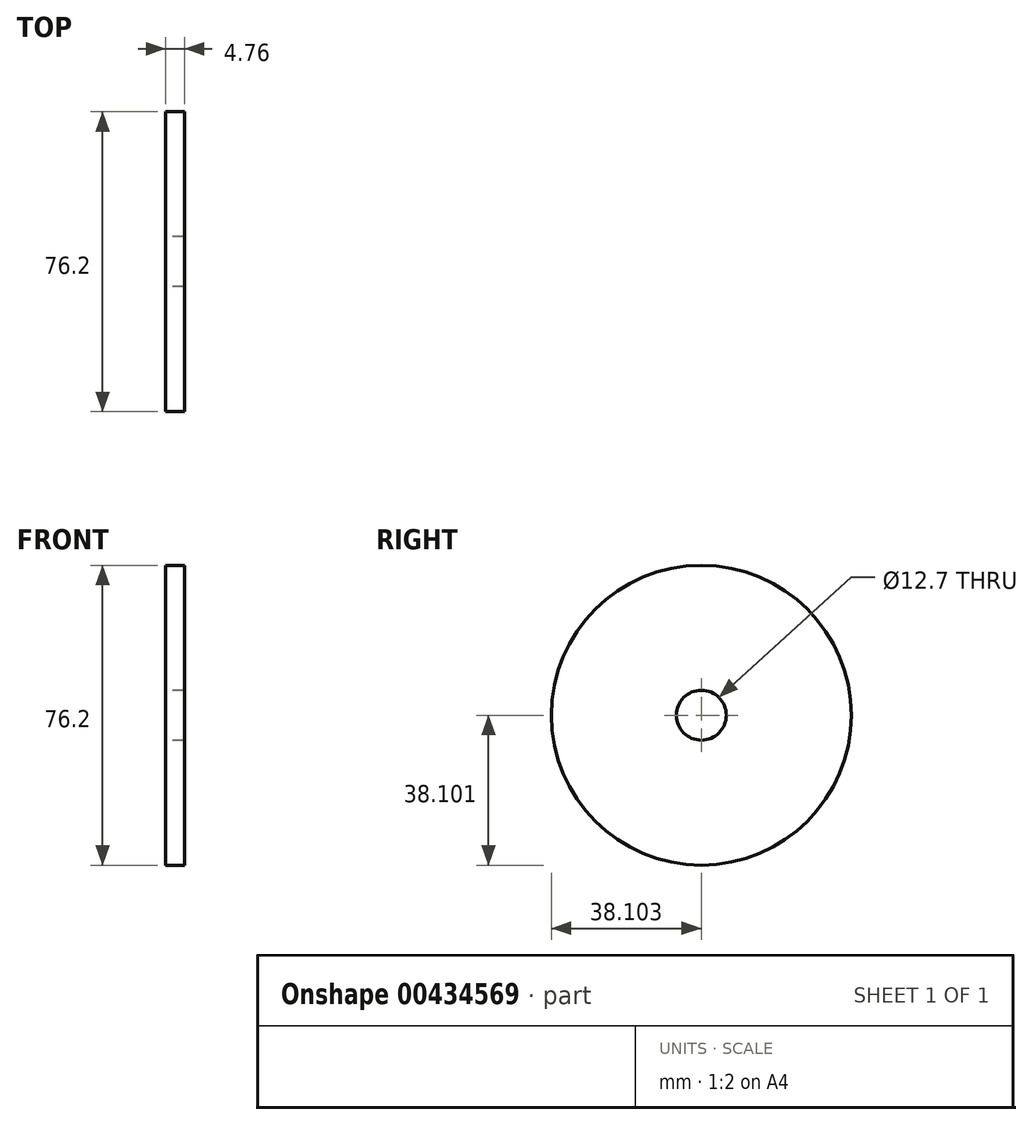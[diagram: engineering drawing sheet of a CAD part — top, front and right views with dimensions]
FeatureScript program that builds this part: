
annotation { "Feature Type Name" : "Feature", "Feature Type Description" : "" }
export const myFeature = defineFeature(function(context is Context, id is Id, definition is map)
    precondition{}
    {
        {
            var Q0;
            Q0=qCreatedBy(makeId("Right.planeOp"),FACE);
            var sketch = newSketch(context, id + "F0", { "sketchPlane" : qUnion([Q0])});
            skCircle(sketch, "E0", {"center": v(-31.17, 28.84) * mm, "radius": 38.1 * mm});
            skCircle(sketch, "E1", {"center": v(-31.17, 28.84) * mm, "radius": 6.35 * mm});
            skSolve(sketch);
        }
        {
            var Q0;
            Q0=makeQuery(id+"F0.imprint","IMPRINT",FACE,{"disambiguationData":[TD([[makeQuery(id+"F0.imprint","IMPRINT",EDGE,{"derivedFrom":sQuery(id+"F0.wireOp",EDGE,"E0")}),1.0]])]});
            extrude(context, id + "F1", {"entities" : qUnion([Q0]), "depth" : 4.76 * mm});
        }
    });
